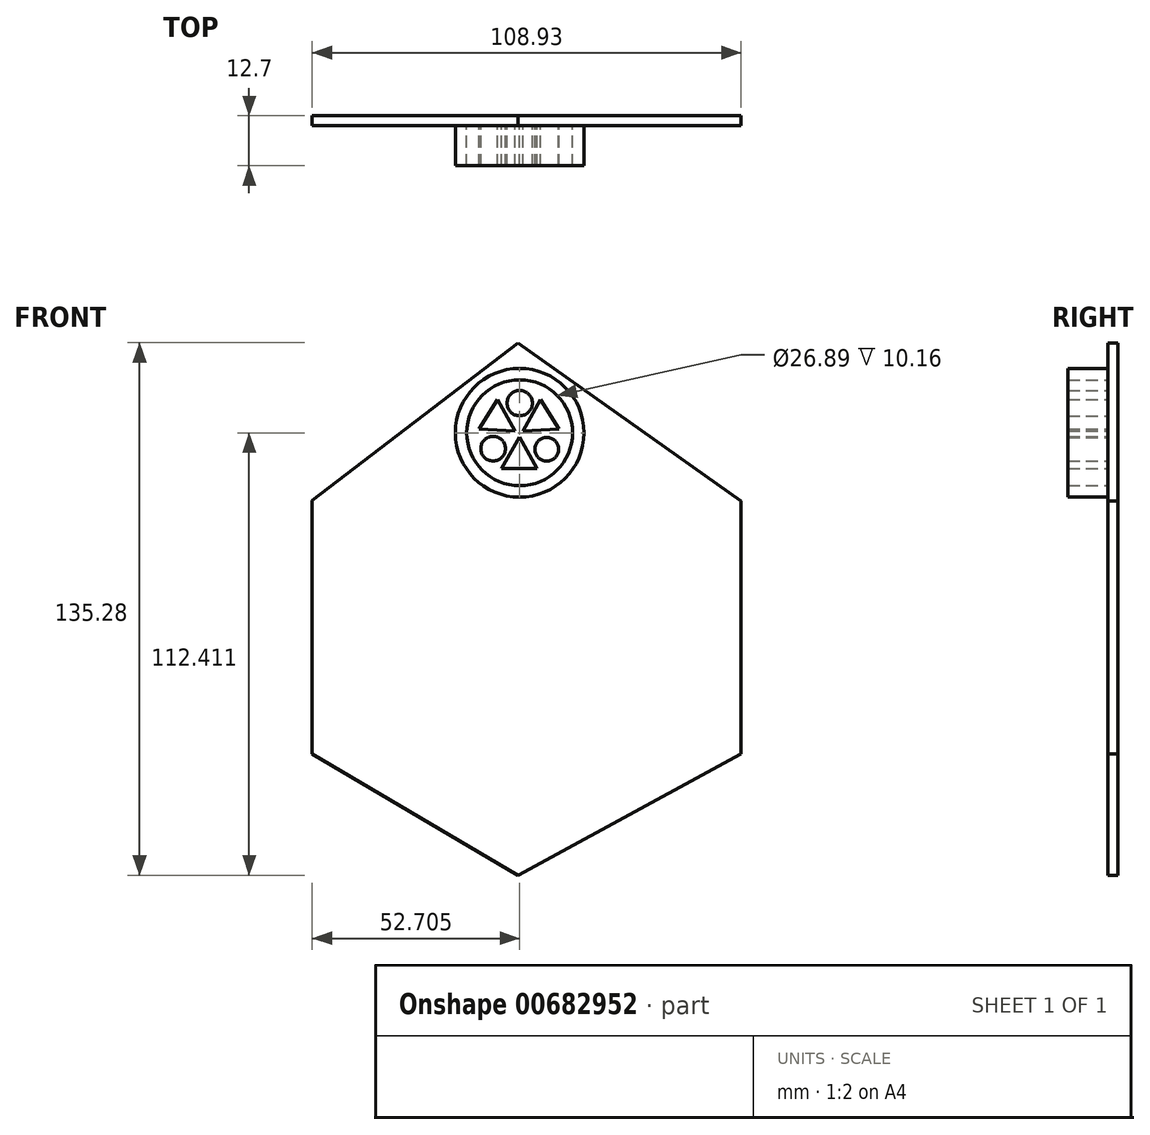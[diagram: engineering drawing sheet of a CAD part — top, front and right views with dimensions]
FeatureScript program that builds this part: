
annotation { "Feature Type Name" : "Feature", "Feature Type Description" : "" }
export const myFeature = defineFeature(function(context is Context, id is Id, definition is map)
    precondition{}
    {
        {
            var Q0;
            Q0=qCreatedBy(makeId("Front.planeOp"),FACE);
            var sketch = newSketch(context, id + "F0", { "sketchPlane" : qUnion([Q0])});
            skLineSegment(sketch, "E0", {"start": v(0, 68.56) * mm, "end": v(59.23, 26.56) * mm});
            skLineSegment(sketch, "E1", {"start": v(59.23, 26.56) * mm, "end": v(59.23, -40.56) * mm});
            skLineSegment(sketch, "E2", {"start": v(59.23, -40.56) * mm, "end": v(0, -72.79) * mm});
            skLineSegment(sketch, "E3", {"start": v(0, -72.79) * mm, "end": v(-54.78, -40.56) * mm});
            skLineSegment(sketch, "E4", {"start": v(-54.78, -40.56) * mm, "end": v(-54.78, 26.56) * mm});
            skLineSegment(sketch, "E5", {"start": v(-54.78, 26.56) * mm, "end": v(0, 68.56) * mm});
            skSolve(sketch);
        }
        {
            var Q0;
            Q0=makeQuery(id+"F0.imprint","IMPRINT",FACE,{"disambiguationData":[TD([[makeQuery(id+"F0.imprint","IMPRINT",EDGE,{"derivedFrom":sQuery(id+"F0.wireOp",EDGE,"E0")}),-1.0]])]});
            extrude(context, id + "F1", {"entities" : qUnion([Q0]), "depth" : 12.7 * mm, "offsetDistance" : 25.4 * mm});
        }
        {
            var Q0;
            Q0=makeQuery(id+"F1.opExtrude","CAP_FACE",FACE,{"disambiguationData":[OSD([sQuery(id+"F0.wireOp",EDGE,"E0"),sQuery(id+"F0.wireOp",EDGE,"E1"),sQuery(id+"F0.wireOp",EDGE,"E2"),sQuery(id+"F0.wireOp",EDGE,"E3"),sQuery(id+"F0.wireOp",EDGE,"E4"),sQuery(id+"F0.wireOp",EDGE,"E5")])],"isStart":false});
            extrude(context, id + "F2", {"entities" : qUnion([Q0]), "operationType" : NewBodyOperationType.REMOVE, "oppositeDirection" : true, "depth" : 2.54 * mm, "offsetDistance" : 25.4 * mm});
        }
        {
            var Q0;
            Q0=makeQuery(id+"F2.boolean.opBoolean","COPY",FACE,{"derivedFrom":makeQuery(id+"F2.opExtrude","CAP_FACE",FACE,{"disambiguationData":[OSD([sQuery(id+"F0.wireOp",EDGE,"E0"),sQuery(id+"F0.wireOp",EDGE,"E1"),sQuery(id+"F0.wireOp",EDGE,"E2"),sQuery(id+"F0.wireOp",EDGE,"E3"),sQuery(id+"F0.wireOp",EDGE,"E4"),sQuery(id+"F0.wireOp",EDGE,"E5")])],"isStart":false})});
            extrude(context, id + "F3", {"entities" : qUnion([Q0]), "operationType" : NewBodyOperationType.REMOVE, "oppositeDirection" : true, "depth" : 7.62 * mm, "offsetDistance" : 25.4 * mm});
        }
        {
            var Q0;
            Q0=makeQuery(id+"F1.opExtrude","SWEPT_FACE",FACE,{"disambiguationData":[OSD([sQuery(id+"F0.wireOp",EDGE,"E0")])]});
            extrude(context, id + "F4", {"entities" : qUnion([Q0]), "operationType" : NewBodyOperationType.REMOVE, "oppositeDirection" : true, "depth" : 2.54 * mm, "offsetDistance" : 25.4 * mm});
        }
        {
            var Q0;
            Q0=makeQuery(id+"F1.opExtrude","SWEPT_FACE",FACE,{"disambiguationData":[OSD([sQuery(id+"F0.wireOp",EDGE,"E5")])]});
            extrude(context, id + "F5", {"entities" : qUnion([Q0]), "operationType" : NewBodyOperationType.REMOVE, "oppositeDirection" : true, "depth" : 2.54 * mm, "offsetDistance" : 25.4 * mm});
        }
        {
            var Q0;
            Q0=makeQuery(id+"F1.opExtrude","SWEPT_FACE",FACE,{"disambiguationData":[OSD([sQuery(id+"F0.wireOp",EDGE,"E1")])]});
            extrude(context, id + "F6", {"entities" : qUnion([Q0]), "operationType" : NewBodyOperationType.REMOVE, "oppositeDirection" : true, "depth" : 2.54 * mm, "offsetDistance" : 25.4 * mm});
        }
        {
            var Q0;
            Q0=makeQuery(id+"F1.opExtrude","SWEPT_FACE",FACE,{"disambiguationData":[OSD([sQuery(id+"F0.wireOp",EDGE,"E4")])]});
            extrude(context, id + "F7", {"entities" : qUnion([Q0]), "operationType" : NewBodyOperationType.REMOVE, "oppositeDirection" : true, "depth" : 2.54 * mm, "offsetDistance" : 25.4 * mm});
        }
        {
            var Q0;
            Q0=makeQuery(id+"F1.opExtrude","SWEPT_FACE",FACE,{"disambiguationData":[OSD([sQuery(id+"F0.wireOp",EDGE,"E3")])]});
            extrude(context, id + "F8", {"entities" : qUnion([Q0]), "operationType" : NewBodyOperationType.REMOVE, "oppositeDirection" : true, "depth" : 2.54 * mm, "offsetDistance" : 25.4 * mm});
        }
        {
            var Q0;
            Q0=makeQuery(id+"F1.opExtrude","SWEPT_FACE",FACE,{"disambiguationData":[OSD([sQuery(id+"F0.wireOp",EDGE,"E2")])]});
            extrude(context, id + "F9", {"entities" : qUnion([Q0]), "operationType" : NewBodyOperationType.REMOVE, "oppositeDirection" : true, "depth" : 2.54 * mm, "offsetDistance" : 25.4 * mm});
        }
        {
            var Q0;
            Q0=makeQuery(id+"F3.boolean.opBoolean","COPY",FACE,{"derivedFrom":makeQuery(id+"F3.opExtrude","CAP_FACE",FACE,{"disambiguationData":[OSD([sQuery(id+"F0.wireOp",EDGE,"E0"),sQuery(id+"F0.wireOp",EDGE,"E1"),sQuery(id+"F0.wireOp",EDGE,"E2"),sQuery(id+"F0.wireOp",EDGE,"E3"),sQuery(id+"F0.wireOp",EDGE,"E4"),sQuery(id+"F0.wireOp",EDGE,"E5")])],"isStart":false})});
            var sketch = newSketch(context, id + "F10", { "sketchPlane" : qUnion([Q0])});
            skCircle(sketch, "E6", {"center": v(0.47, 42.54) * mm, "radius": 16.34 * mm});
            skCircle(sketch, "E7", {"center": v(0.47, 42.54) * mm, "radius": 13.45 * mm});
            skCircle(sketch, "E8", {"center": v(0.47, 50.07) * mm, "radius": 3.22 * mm});
            skCircle(sketch, "E9", {"center": v(7.33, 38.35) * mm, "radius": 3.02 * mm});
            skCircle(sketch, "E10", {"center": v(-6.28, 38.51) * mm, "radius": 3.14 * mm});
            skLineSegment(sketch, "E11", {"start": v(-9.8, 43.55) * mm, "end": v(-5.22, 50.94) * mm});
            skLineSegment(sketch, "E12", {"start": v(-5.22, 50.94) * mm, "end": v(-0.7, 43.01) * mm});
            skLineSegment(sketch, "E13", {"start": v(-0.7, 43.01) * mm, "end": v(-9.8, 43.55) * mm});
            skLineSegment(sketch, "E14", {"start": v(1.3, 43.02) * mm, "end": v(5.76, 51.02) * mm});
            skLineSegment(sketch, "E15", {"start": v(5.76, 51.02) * mm, "end": v(10.5, 43.55) * mm});
            skLineSegment(sketch, "E16", {"start": v(10.5, 43.55) * mm, "end": v(1.3, 43.02) * mm});
            skLineSegment(sketch, "E17", {"start": v(0.39, 41.42) * mm, "end": v(4.87, 33.42) * mm});
            skLineSegment(sketch, "E18", {"start": v(4.87, 33.42) * mm, "end": v(-4.1, 33.42) * mm});
            skLineSegment(sketch, "E19", {"start": v(-4.1, 33.42) * mm, "end": v(0.39, 41.42) * mm});
            skSolve(sketch);
        }
        {
            var Q0;
            Q0=makeQuery(id+"F10.imprint","IMPRINT",FACE,{"disambiguationData":[TD([[makeQuery(id+"F10.imprint","IMPRINT",EDGE,{"derivedFrom":sQuery(id+"F10.wireOp",EDGE,"E6")}),1.0]])]});
            var Q1;
            Q1=makeQuery(id+"F10.imprint","IMPRINT",FACE,{"disambiguationData":[TD([[makeQuery(id+"F10.imprint","IMPRINT",EDGE,{"derivedFrom":sQuery(id+"F10.wireOp",EDGE,"E14")}),-1.0]])]});
            var Q2;
            Q2=makeQuery(id+"F10.imprint","IMPRINT",FACE,{"disambiguationData":[TD([[makeQuery(id+"F10.imprint","IMPRINT",EDGE,{"derivedFrom":sQuery(id+"F10.wireOp",EDGE,"E9")}),1.0]])]});
            var Q3;
            Q3=makeQuery(id+"F10.imprint","IMPRINT",FACE,{"disambiguationData":[TD([[makeQuery(id+"F10.imprint","IMPRINT",EDGE,{"derivedFrom":sQuery(id+"F10.wireOp",EDGE,"E17")}),-1.0]])]});
            var Q4;
            Q4=makeQuery(id+"F10.imprint","IMPRINT",FACE,{"disambiguationData":[TD([[makeQuery(id+"F10.imprint","IMPRINT",EDGE,{"derivedFrom":sQuery(id+"F10.wireOp",EDGE,"E10")}),1.0]])]});
            var Q5;
            Q5=makeQuery(id+"F10.imprint","IMPRINT",FACE,{"disambiguationData":[TD([[makeQuery(id+"F10.imprint","IMPRINT",EDGE,{"derivedFrom":sQuery(id+"F10.wireOp",EDGE,"E11")}),-1.0]])]});
            var Q6;
            Q6=makeQuery(id+"F10.imprint","IMPRINT",FACE,{"disambiguationData":[TD([[makeQuery(id+"F10.imprint","IMPRINT",EDGE,{"derivedFrom":sQuery(id+"F10.wireOp",EDGE,"E8")}),1.0]])]});
            extrude(context, id + "F11", {"entities" : qUnion([Q0, Q1, Q2, Q3, Q4, Q5, Q6]), "operationType" : NewBodyOperationType.ADD, "depth" : 25.4 * mm, "offsetDistance" : 25.4 * mm});
        }
        {
            var Q0;
            Q0=makeQuery(id+"F11.opExtrude","CAP_FACE",FACE,{"disambiguationData":[OSD([sQuery(id+"F10.wireOp",EDGE,"E6"),sQuery(id+"F10.wireOp",EDGE,"E7")])],"isStart":false});
            var Q1;
            Q1=makeQuery(id+"F11.opExtrude","CAP_FACE",FACE,{"disambiguationData":[OSD([sQuery(id+"F10.wireOp",EDGE,"E17"),sQuery(id+"F10.wireOp",EDGE,"E18"),sQuery(id+"F10.wireOp",EDGE,"E19")])],"isStart":false});
            var Q2;
            Q2=makeQuery(id+"F11.opExtrude","CAP_FACE",FACE,{"disambiguationData":[OSD([sQuery(id+"F10.wireOp",EDGE,"E9")])],"isStart":false});
            var Q3;
            Q3=makeQuery(id+"F11.opExtrude","CAP_FACE",FACE,{"disambiguationData":[OSD([sQuery(id+"F10.wireOp",EDGE,"E14"),sQuery(id+"F10.wireOp",EDGE,"E15"),sQuery(id+"F10.wireOp",EDGE,"E16")])],"isStart":false});
            var Q4;
            Q4=makeQuery(id+"F11.opExtrude","CAP_FACE",FACE,{"disambiguationData":[OSD([sQuery(id+"F10.wireOp",EDGE,"E11"),sQuery(id+"F10.wireOp",EDGE,"E12"),sQuery(id+"F10.wireOp",EDGE,"E13")])],"isStart":false});
            var Q5;
            Q5=makeQuery(id+"F11.opExtrude","CAP_FACE",FACE,{"disambiguationData":[OSD([sQuery(id+"F10.wireOp",EDGE,"E10")])],"isStart":false});
            var Q6;
            Q6=makeQuery(id+"F11.opExtrude","CAP_FACE",FACE,{"disambiguationData":[OSD([sQuery(id+"F10.wireOp",EDGE,"E8")])],"isStart":false});
            extrude(context, id + "F12", {"entities" : qUnion([Q0, Q1, Q2, Q3, Q4, Q5, Q6]), "operationType" : NewBodyOperationType.REMOVE, "oppositeDirection" : true, "depth" : 19.05 * mm, "offsetDistance" : 25.4 * mm});
        }
        {
            var Q0;
            Q0=makeQuery(id+"F12.boolean.opBoolean","COPY",FACE,{"derivedFrom":makeQuery(id+"F12.opExtrude","CAP_FACE",FACE,{"disambiguationData":[OSD([sQuery(id+"F10.wireOp",EDGE,"E6"),sQuery(id+"F10.wireOp",EDGE,"E7")])],"isStart":false})});
            var Q1;
            Q1=makeQuery(id+"F12.boolean.opBoolean","COPY",FACE,{"derivedFrom":makeQuery(id+"F12.opExtrude","CAP_FACE",FACE,{"disambiguationData":[OSD([sQuery(id+"F10.wireOp",EDGE,"E9")])],"isStart":false})});
            var Q2;
            Q2=makeQuery(id+"F12.boolean.opBoolean","COPY",FACE,{"derivedFrom":makeQuery(id+"F12.opExtrude","CAP_FACE",FACE,{"disambiguationData":[OSD([sQuery(id+"F10.wireOp",EDGE,"E14"),sQuery(id+"F10.wireOp",EDGE,"E15"),sQuery(id+"F10.wireOp",EDGE,"E16")])],"isStart":false})});
            var Q3;
            Q3=makeQuery(id+"F12.boolean.opBoolean","COPY",FACE,{"derivedFrom":makeQuery(id+"F12.opExtrude","CAP_FACE",FACE,{"disambiguationData":[OSD([sQuery(id+"F10.wireOp",EDGE,"E8")])],"isStart":false})});
            var Q4;
            Q4=makeQuery(id+"F12.boolean.opBoolean","COPY",FACE,{"derivedFrom":makeQuery(id+"F12.opExtrude","CAP_FACE",FACE,{"disambiguationData":[OSD([sQuery(id+"F10.wireOp",EDGE,"E11"),sQuery(id+"F10.wireOp",EDGE,"E12"),sQuery(id+"F10.wireOp",EDGE,"E13")])],"isStart":false})});
            var Q5;
            Q5=makeQuery(id+"F12.boolean.opBoolean","COPY",FACE,{"derivedFrom":makeQuery(id+"F12.opExtrude","CAP_FACE",FACE,{"disambiguationData":[OSD([sQuery(id+"F10.wireOp",EDGE,"E10")])],"isStart":false})});
            var Q6;
            Q6=makeQuery(id+"F12.boolean.opBoolean","COPY",FACE,{"derivedFrom":makeQuery(id+"F12.opExtrude","CAP_FACE",FACE,{"disambiguationData":[OSD([sQuery(id+"F10.wireOp",EDGE,"E17"),sQuery(id+"F10.wireOp",EDGE,"E18"),sQuery(id+"F10.wireOp",EDGE,"E19")])],"isStart":false})});
            extrude(context, id + "F13", {"entities" : qUnion([Q0, Q1, Q2, Q3, Q4, Q5, Q6]), "operationType" : NewBodyOperationType.ADD, "depth" : 6.35 * mm, "offsetDistance" : 25.4 * mm});
        }
        {
            var Q0;
            Q0=makeQuery(id+"F13.opExtrude","CAP_FACE",FACE,{"disambiguationData":[OSD([sQuery(id+"F10.wireOp",EDGE,"E6"),sQuery(id+"F10.wireOp",EDGE,"E7")])],"isStart":false});
            var Q1;
            Q1=makeQuery(id+"F13.opExtrude","CAP_FACE",FACE,{"disambiguationData":[OSD([sQuery(id+"F10.wireOp",EDGE,"E9")])],"isStart":false});
            var Q2;
            Q2=makeQuery(id+"F13.opExtrude","CAP_FACE",FACE,{"disambiguationData":[OSD([sQuery(id+"F10.wireOp",EDGE,"E14"),sQuery(id+"F10.wireOp",EDGE,"E15"),sQuery(id+"F10.wireOp",EDGE,"E16")])],"isStart":false});
            var Q3;
            Q3=makeQuery(id+"F13.opExtrude","CAP_FACE",FACE,{"disambiguationData":[OSD([sQuery(id+"F10.wireOp",EDGE,"E8")])],"isStart":false});
            var Q4;
            Q4=makeQuery(id+"F13.opExtrude","CAP_FACE",FACE,{"disambiguationData":[OSD([sQuery(id+"F10.wireOp",EDGE,"E11"),sQuery(id+"F10.wireOp",EDGE,"E12"),sQuery(id+"F10.wireOp",EDGE,"E13")])],"isStart":false});
            var Q5;
            Q5=makeQuery(id+"F13.opExtrude","CAP_FACE",FACE,{"disambiguationData":[OSD([sQuery(id+"F10.wireOp",EDGE,"E10")])],"isStart":false});
            var Q6;
            Q6=makeQuery(id+"F13.opExtrude","CAP_FACE",FACE,{"disambiguationData":[OSD([sQuery(id+"F10.wireOp",EDGE,"E17"),sQuery(id+"F10.wireOp",EDGE,"E18"),sQuery(id+"F10.wireOp",EDGE,"E19")])],"isStart":false});
            extrude(context, id + "F14", {"entities" : qUnion([Q0, Q1, Q2, Q3, Q4, Q5, Q6]), "operationType" : NewBodyOperationType.REMOVE, "oppositeDirection" : true, "depth" : 2.54 * mm, "offsetDistance" : 25.4 * mm});
        }
        {
            var Q0;
            Q0=makeQuery(id+"F14.boolean.opBoolean","COPY",FACE,{"derivedFrom":makeQuery(id+"F14.opExtrude","CAP_FACE",FACE,{"disambiguationData":[OSD([sQuery(id+"F10.wireOp",EDGE,"E14"),sQuery(id+"F10.wireOp",EDGE,"E15"),sQuery(id+"F10.wireOp",EDGE,"E16")])],"isStart":false})});
            var Q1;
            Q1=makeQuery(id+"F14.boolean.opBoolean","COPY",FACE,{"derivedFrom":makeQuery(id+"F14.opExtrude","CAP_FACE",FACE,{"disambiguationData":[OSD([sQuery(id+"F10.wireOp",EDGE,"E8")])],"isStart":false})});
            var Q2;
            Q2=makeQuery(id+"F14.boolean.opBoolean","COPY",FACE,{"derivedFrom":makeQuery(id+"F14.opExtrude","CAP_FACE",FACE,{"disambiguationData":[OSD([sQuery(id+"F10.wireOp",EDGE,"E9")])],"isStart":false})});
            var Q3;
            Q3=makeQuery(id+"F14.boolean.opBoolean","COPY",FACE,{"derivedFrom":makeQuery(id+"F14.opExtrude","CAP_FACE",FACE,{"disambiguationData":[OSD([sQuery(id+"F10.wireOp",EDGE,"E17"),sQuery(id+"F10.wireOp",EDGE,"E18"),sQuery(id+"F10.wireOp",EDGE,"E19")])],"isStart":false})});
            var Q4;
            Q4=makeQuery(id+"F14.boolean.opBoolean","COPY",FACE,{"derivedFrom":makeQuery(id+"F14.opExtrude","CAP_FACE",FACE,{"disambiguationData":[OSD([sQuery(id+"F10.wireOp",EDGE,"E11"),sQuery(id+"F10.wireOp",EDGE,"E12"),sQuery(id+"F10.wireOp",EDGE,"E13")])],"isStart":false})});
            var Q5;
            Q5=makeQuery(id+"F14.boolean.opBoolean","COPY",FACE,{"derivedFrom":makeQuery(id+"F14.opExtrude","CAP_FACE",FACE,{"disambiguationData":[OSD([sQuery(id+"F10.wireOp",EDGE,"E10")])],"isStart":false})});
            var Q6;
            Q6=makeQuery(id+"F14.boolean.opBoolean","COPY",FACE,{"derivedFrom":makeQuery(id+"F14.opExtrude","CAP_FACE",FACE,{"disambiguationData":[OSD([sQuery(id+"F10.wireOp",EDGE,"E6"),sQuery(id+"F10.wireOp",EDGE,"E7")])],"isStart":false})});
            extrude(context, id + "F15", {"entities" : qUnion([Q0, Q1, Q2, Q3, Q4, Q5, Q6]), "operationType" : NewBodyOperationType.REMOVE, "oppositeDirection" : true, "depth" : 2.54 * mm, "offsetDistance" : 25.4 * mm});
        }
        {
            var Q0;
            Q0=makeQuery(id+"F15.boolean.opBoolean","COPY",FACE,{"derivedFrom":makeQuery(id+"F15.opExtrude","CAP_FACE",FACE,{"disambiguationData":[OSD([sQuery(id+"F10.wireOp",EDGE,"E8")])],"isStart":false})});
            var Q1;
            Q1=makeQuery(id+"F15.boolean.opBoolean","COPY",FACE,{"derivedFrom":makeQuery(id+"F15.opExtrude","CAP_FACE",FACE,{"disambiguationData":[OSD([sQuery(id+"F10.wireOp",EDGE,"E14"),sQuery(id+"F10.wireOp",EDGE,"E15"),sQuery(id+"F10.wireOp",EDGE,"E16")])],"isStart":false})});
            var Q2;
            Q2=makeQuery(id+"F15.boolean.opBoolean","COPY",FACE,{"derivedFrom":makeQuery(id+"F15.opExtrude","CAP_FACE",FACE,{"disambiguationData":[OSD([sQuery(id+"F10.wireOp",EDGE,"E9")])],"isStart":false})});
            var Q3;
            Q3=makeQuery(id+"F15.boolean.opBoolean","COPY",FACE,{"derivedFrom":makeQuery(id+"F15.opExtrude","CAP_FACE",FACE,{"disambiguationData":[OSD([sQuery(id+"F10.wireOp",EDGE,"E17"),sQuery(id+"F10.wireOp",EDGE,"E18"),sQuery(id+"F10.wireOp",EDGE,"E19")])],"isStart":false})});
            var Q4;
            Q4=makeQuery(id+"F15.boolean.opBoolean","COPY",FACE,{"derivedFrom":makeQuery(id+"F15.opExtrude","CAP_FACE",FACE,{"disambiguationData":[OSD([sQuery(id+"F10.wireOp",EDGE,"E11"),sQuery(id+"F10.wireOp",EDGE,"E12"),sQuery(id+"F10.wireOp",EDGE,"E13")])],"isStart":false})});
            var Q5;
            Q5=makeQuery(id+"F15.boolean.opBoolean","COPY",FACE,{"derivedFrom":makeQuery(id+"F15.opExtrude","CAP_FACE",FACE,{"disambiguationData":[OSD([sQuery(id+"F10.wireOp",EDGE,"E10")])],"isStart":false})});
            var Q6;
            Q6=makeQuery(id+"F15.boolean.opBoolean","COPY",FACE,{"derivedFrom":makeQuery(id+"F15.opExtrude","CAP_FACE",FACE,{"disambiguationData":[OSD([sQuery(id+"F10.wireOp",EDGE,"E6"),sQuery(id+"F10.wireOp",EDGE,"E7")])],"isStart":false})});
            extrude(context, id + "F16", {"entities" : qUnion([Q0, Q1, Q2, Q3, Q4, Q5, Q6]), "operationType" : NewBodyOperationType.ADD, "depth" : 2.54 * mm, "offsetDistance" : 25.4 * mm});
        }
    });
